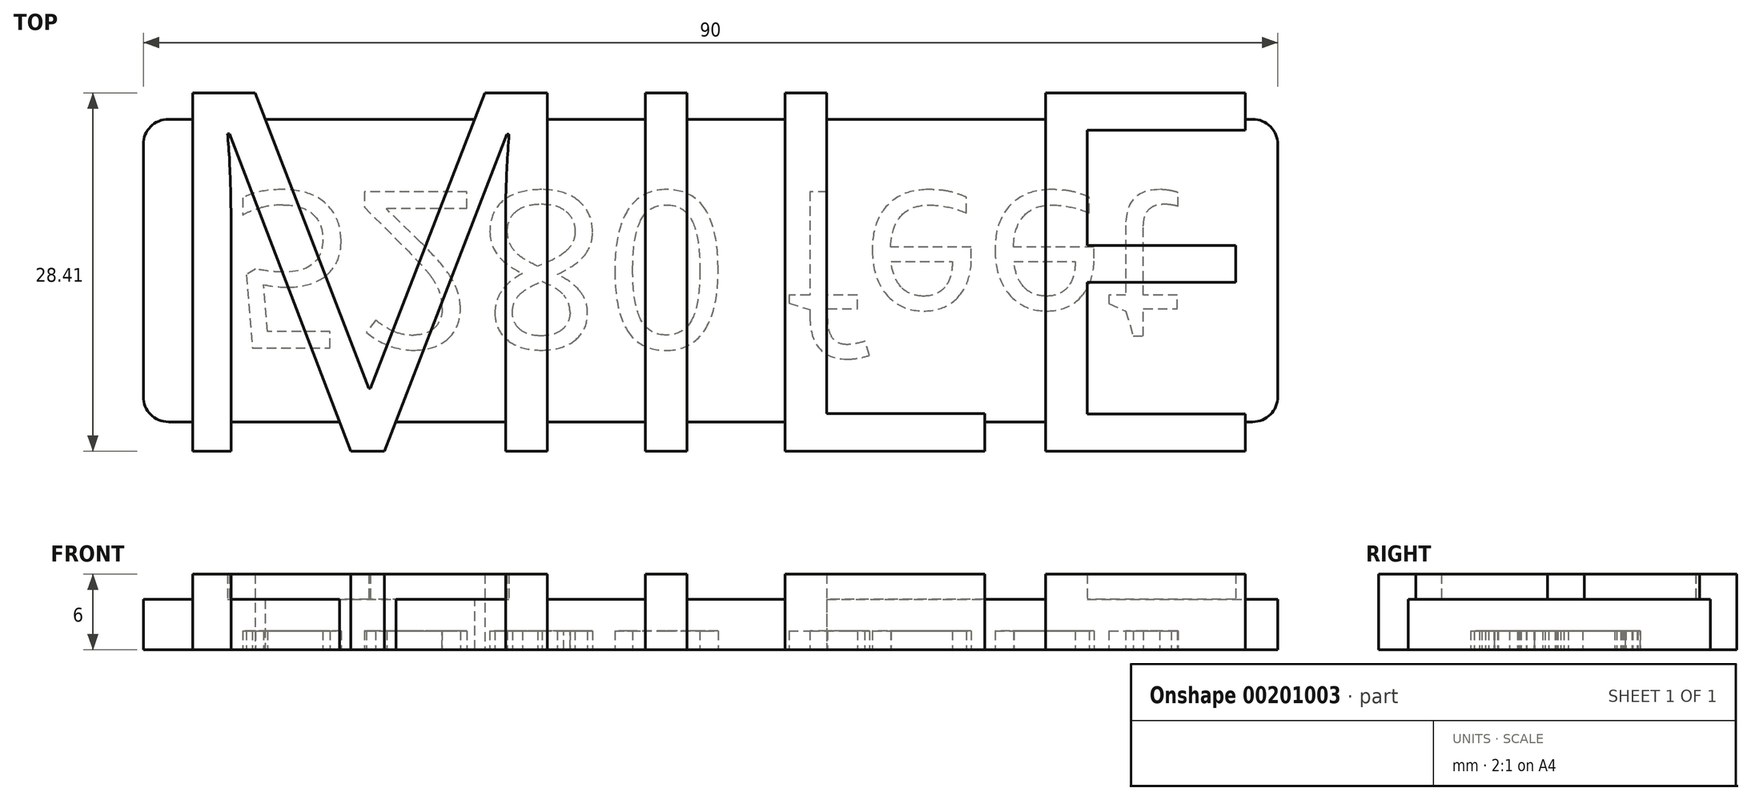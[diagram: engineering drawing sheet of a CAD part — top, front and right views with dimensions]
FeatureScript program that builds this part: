
annotation { "Feature Type Name" : "Feature", "Feature Type Description" : "" }
export const myFeature = defineFeature(function(context is Context, id is Id, definition is map)
    precondition{}
    {
        {
            var Q0;
            Q0=qCreatedBy(makeId("Top.planeOp"),FACE);
            var sketch = newSketch(context, id + "F0", { "sketchPlane" : qUnion([Q0])});
            skLineSegment(sketch, "E0.bottom", {"start": v(-45, 12) * mm, "end": v(45, 12) * mm});
            skLineSegment(sketch, "E0.top", {"start": v(-45, -12) * mm, "end": v(45, -12) * mm});
            skLineSegment(sketch, "E0.left", {"start": v(-45, 12) * mm, "end": v(-45, -12) * mm});
            skLineSegment(sketch, "E0.right", {"start": v(45, 12) * mm, "end": v(45, -12) * mm});
            skLineSegment(sketch, "E1", {"start": v(0, -12) * mm, "end": v(0, 12) * mm, "construction": true});
            skSolve(sketch);
        }
        {
            var Q0;
            Q0=makeQuery(id+"F0.imprint","IMPRINT",FACE,{"disambiguationData":[TD([[makeQuery(id+"F0.imprint","IMPRINT",EDGE,{"derivedFrom":sQuery(id+"F0.wireOp",EDGE,"E0.bottom")}),-1.0]])]});
            extrude(context, id + "F1", {"entities" : qUnion([Q0]), "depth" : 4 * mm});
        }
        {
            var Q0;
            Q0=makeQuery(id+"F1.opExtrude","SWEPT_EDGE",EDGE,{"disambiguationData":[OSD([sQuery(id+"F0.wireOp",EDGE,"E0.top"),sQuery(id+"F0.wireOp",EDGE,"E0.left")])]});
            var Q1;
            Q1=makeQuery(id+"F1.opExtrude","SWEPT_EDGE",EDGE,{"disambiguationData":[OSD([sQuery(id+"F0.wireOp",EDGE,"E0.bottom"),sQuery(id+"F0.wireOp",EDGE,"E0.right")])]});
            var Q2;
            Q2=makeQuery(id+"F1.opExtrude","SWEPT_EDGE",EDGE,{"disambiguationData":[OSD([sQuery(id+"F0.wireOp",EDGE,"E0.bottom"),sQuery(id+"F0.wireOp",EDGE,"E0.left")])]});
            var Q3;
            Q3=makeQuery(id+"F1.opExtrude","SWEPT_EDGE",EDGE,{"disambiguationData":[OSD([sQuery(id+"F0.wireOp",EDGE,"E0.top"),sQuery(id+"F0.wireOp",EDGE,"E0.right")])]});
            fillet(context, id + "F2", {"entities" : qUnion([Q0, Q1, Q2, Q3]), "radius" : 2 * mm, "tangentPropagation" : true, "allowEdgeOverflow" : false});
        }
        {
            var Q0;
            Q0=makeQuery(id+"F1.opExtrude","CAP_FACE",FACE,{"disambiguationData":[OSD([sQuery(id+"F0.wireOp",EDGE,"E0.bottom"),sQuery(id+"F0.wireOp",EDGE,"E0.top"),sQuery(id+"F0.wireOp",EDGE,"E0.left"),sQuery(id+"F0.wireOp",EDGE,"E0.right")])],"isStart":false});
            var sketch = newSketch(context, id + "F3", { "sketchPlane" : qUnion([Q0])});
            skText(sketch, "E2", { "text": "MILE", "fontName": "OpenSans-Regular.ttf"});
            const initialGuessF3  = {"E2": [-0.045, -0.01433, 1, 0, 0.02865]};
            skSetInitialGuess(sketch, initialGuessF3);
            skSolve(sketch);
        }
        {
            var Q0;
            {var subQ0=sQuery(id+"F3.wireOp",EDGE,"E2.sketch_text.stroke-4");Q0=makeQuery(id+"F3.imprint","IMPRINT",FACE,{"disambiguationData":[TD([[makeQuery(id+"F3.imprint","IMPRINT",EDGE,{"derivedFrom":subQ0}),-1.0]])]});}
            var Q1;
            {var subQ0=sQuery(id+"F3.wireOp",EDGE,"E2.sketch_text.stroke-3");var subQ1=sQuery(id+"F3.wireOp",EDGE,"E2.sketch_text.stroke-2");var subQ2=makeQuery(id+"F3.imprint","INTERSECT",VERTEX,{"derivedFrom":[subQ1,subQ0]});Q1=makeQuery(id+"F3.imprint","IMPRINT",FACE,{"disambiguationData":[TD([[makeQuery(id+"F3.imprint","IMPRINT",EDGE,{"disambiguationData":[TD([[subQ2,1.0]])],"derivedFrom":subQ1}),-1.0]])]});}
            var Q2;
            {var subQ1=sQuery(id+"F3.wireOp",EDGE,"E2.sketch_text.stroke-1");Q2=makeQuery(id+"F3.imprint","IMPRINT",FACE,{"disambiguationData":[TD([[makeQuery(id+"F3.imprint","IMPRINT",EDGE,{"derivedFrom":subQ1}),-1.0]])]});}
            var Q3;
            {var subQ0=sQuery(id+"F3.wireOp",EDGE,"E2.sketch_text.stroke-0");var subQ1=makeQuery(id+"F1.opExtrude","CAP_EDGE",EDGE,{"disambiguationData":[OSD([sQuery(id+"F0.wireOp",EDGE,"E0.top")])],"isStart":false});var subQ2=makeQuery(id+"F3.imprint","INTERSECT",VERTEX,{"derivedFrom":[subQ1,subQ0]});Q3=makeQuery(id+"F3.imprint","IMPRINT",FACE,{"disambiguationData":[TD([[makeQuery(id+"F3.imprint","IMPRINT",EDGE,{"disambiguationData":[TD([[subQ2,-1.0]])],"derivedFrom":subQ0}),-1.0]])]});}
            var Q4;
            {var subQ1=sQuery(id+"F3.wireOp",EDGE,"E2.sketch_text.stroke-8");Q4=makeQuery(id+"F3.imprint","IMPRINT",FACE,{"disambiguationData":[TD([[makeQuery(id+"F3.imprint","IMPRINT",EDGE,{"derivedFrom":subQ1}),-1.0]])]});}
            var Q5;
            {var subQ0=sQuery(id+"F3.wireOp",EDGE,"E2.sketch_text.stroke-9");var subQ1=makeQuery(id+"F1.opExtrude","CAP_EDGE",EDGE,{"disambiguationData":[OSD([sQuery(id+"F0.wireOp",EDGE,"E0.bottom")])],"isStart":false});var subQ2=makeQuery(id+"F3.imprint","INTERSECT",VERTEX,{"derivedFrom":[subQ1,subQ0]});Q5=makeQuery(id+"F3.imprint","IMPRINT",FACE,{"disambiguationData":[TD([[makeQuery(id+"F3.imprint","IMPRINT",EDGE,{"disambiguationData":[TD([[subQ2,1.0]])],"derivedFrom":subQ0}),-1.0]])]});}
            var Q6;
            {var subQ1=sQuery(id+"F3.wireOp",EDGE,"E2.sketch_text.stroke-10");Q6=makeQuery(id+"F3.imprint","IMPRINT",FACE,{"disambiguationData":[TD([[makeQuery(id+"F3.imprint","IMPRINT",EDGE,{"derivedFrom":subQ1}),-1.0]])]});}
            var Q7;
            {var subQ0=sQuery(id+"F3.wireOp",EDGE,"E2.sketch_text.stroke-11");var subQ1=makeQuery(id+"F1.opExtrude","CAP_EDGE",EDGE,{"disambiguationData":[OSD([sQuery(id+"F0.wireOp",EDGE,"E0.bottom")])],"isStart":false});var subQ2=makeQuery(id+"F3.imprint","INTERSECT",VERTEX,{"derivedFrom":[subQ1,subQ0]});Q7=makeQuery(id+"F3.imprint","IMPRINT",FACE,{"disambiguationData":[TD([[makeQuery(id+"F3.imprint","IMPRINT",EDGE,{"disambiguationData":[TD([[subQ2,-1.0]])],"derivedFrom":subQ0}),-1.0]])]});}
            var Q8;
            {var subQ0=sQuery(id+"F3.wireOp",EDGE,"E2.sketch_text.stroke-12");Q8=makeQuery(id+"F3.imprint","IMPRINT",FACE,{"disambiguationData":[TD([[makeQuery(id+"F3.imprint","IMPRINT",EDGE,{"derivedFrom":subQ0}),-1.0]])]});}
            var Q9;
            {var subQ0=sQuery(id+"F3.wireOp",EDGE,"E2.sketch_text.stroke-21");Q9=makeQuery(id+"F3.imprint","IMPRINT",FACE,{"disambiguationData":[TD([[makeQuery(id+"F3.imprint","IMPRINT",EDGE,{"derivedFrom":subQ0}),-1.0]])]});}
            var Q10;
            {var subQ0=sQuery(id+"F3.wireOp",EDGE,"E2.sketch_text.stroke-18");var subQ1=makeQuery(id+"F1.opExtrude","CAP_EDGE",EDGE,{"disambiguationData":[OSD([sQuery(id+"F0.wireOp",EDGE,"E0.top")])],"isStart":false});var subQ2=makeQuery(id+"F3.imprint","INTERSECT",VERTEX,{"derivedFrom":[subQ1,subQ0]});Q10=makeQuery(id+"F3.imprint","IMPRINT",FACE,{"disambiguationData":[TD([[makeQuery(id+"F3.imprint","IMPRINT",EDGE,{"disambiguationData":[TD([[subQ2,-1.0]])],"derivedFrom":subQ0}),-1.0]])]});}
            var Q11;
            {var subQ0=sQuery(id+"F3.wireOp",EDGE,"E2.sketch_text.stroke-19");Q11=makeQuery(id+"F3.imprint","IMPRINT",FACE,{"disambiguationData":[TD([[makeQuery(id+"F3.imprint","IMPRINT",EDGE,{"derivedFrom":subQ0}),-1.0]])]});}
            var Q12;
            {var subQ0=sQuery(id+"F3.wireOp",EDGE,"E2.sketch_text.stroke-25");Q12=makeQuery(id+"F3.imprint","IMPRINT",FACE,{"disambiguationData":[TD([[makeQuery(id+"F3.imprint","IMPRINT",EDGE,{"derivedFrom":subQ0}),-1.0]])]});}
            var Q13;
            {var subQ0=sQuery(id+"F3.wireOp",EDGE,"E2.sketch_text.stroke-22");var subQ1=makeQuery(id+"F1.opExtrude","CAP_EDGE",EDGE,{"disambiguationData":[OSD([sQuery(id+"F0.wireOp",EDGE,"E0.top")])],"isStart":false});var subQ2=makeQuery(id+"F3.imprint","INTERSECT",VERTEX,{"derivedFrom":[subQ1,subQ0]});Q13=makeQuery(id+"F3.imprint","IMPRINT",FACE,{"disambiguationData":[TD([[makeQuery(id+"F3.imprint","IMPRINT",EDGE,{"disambiguationData":[TD([[subQ2,-1.0]])],"derivedFrom":subQ0}),-1.0]])]});}
            var Q14;
            {var subQ0=sQuery(id+"F3.wireOp",EDGE,"E2.sketch_text.stroke-23");Q14=makeQuery(id+"F3.imprint","IMPRINT",FACE,{"disambiguationData":[TD([[makeQuery(id+"F3.imprint","IMPRINT",EDGE,{"derivedFrom":subQ0}),-1.0]])]});}
            var Q15;
            {var subQ5=sQuery(id+"F3.wireOp",EDGE,"E2.sketch_text.stroke-28");Q15=makeQuery(id+"F3.imprint","IMPRINT",FACE,{"disambiguationData":[TD([[makeQuery(id+"F3.imprint","IMPRINT",EDGE,{"derivedFrom":subQ5}),-1.0]])]});}
            var Q16;
            {var subQ0=sQuery(id+"F3.wireOp",EDGE,"E2.sketch_text.stroke-34");Q16=makeQuery(id+"F3.imprint","IMPRINT",FACE,{"disambiguationData":[TD([[makeQuery(id+"F3.imprint","IMPRINT",EDGE,{"derivedFrom":subQ0}),-1.0]])]});}
            var Q17;
            {var subQ0=sQuery(id+"F3.wireOp",EDGE,"E2.sketch_text.stroke-30");Q17=makeQuery(id+"F3.imprint","IMPRINT",FACE,{"disambiguationData":[TD([[makeQuery(id+"F3.imprint","IMPRINT",EDGE,{"derivedFrom":subQ0}),-1.0]])]});}
            var Q18;
            {var subQ0=sQuery(id+"F3.wireOp",EDGE,"E2.sketch_text.stroke-6");Q18=makeQuery(id+"F3.imprint","IMPRINT",FACE,{"disambiguationData":[TD([[makeQuery(id+"F3.imprint","IMPRINT",EDGE,{"derivedFrom":subQ0}),-1.0]])]});}
            var Q19;
            {var subQ0=sQuery(id+"F3.wireOp",EDGE,"E2.sketch_text.stroke-17");Q19=makeQuery(id+"F3.imprint","IMPRINT",FACE,{"disambiguationData":[TD([[makeQuery(id+"F3.imprint","IMPRINT",EDGE,{"derivedFrom":subQ0}),-1.0]])]});}
            var Q20;
            {var subQ0=sQuery(id+"F3.wireOp",EDGE,"E2.sketch_text.stroke-27");Q20=makeQuery(id+"F3.imprint","IMPRINT",FACE,{"disambiguationData":[TD([[makeQuery(id+"F3.imprint","IMPRINT",EDGE,{"derivedFrom":subQ0}),-1.0]])]});}
            extrude(context, id + "F4", {"entities" : qUnion([Q0, Q1, Q2, Q3, Q4, Q5, Q6, Q7, Q8, Q9, Q10, Q11, Q12, Q13, Q14, Q15, Q16, Q17, Q18, Q19, Q20]), "operationType" : NewBodyOperationType.ADD, "depth" : 2 * mm, "hasSecondDirection" : true, "secondDirectionOppositeDirection" : true, "secondDirectionDepth" : 4 * mm});
        }
        {
            var Q0;
            Q0=makeQuery(id+"F1.opExtrude","CAP_FACE",FACE,{"disambiguationData":[OSD([sQuery(id+"F0.wireOp",EDGE,"E0.bottom"),sQuery(id+"F0.wireOp",EDGE,"E0.top"),sQuery(id+"F0.wireOp",EDGE,"E0.left"),sQuery(id+"F0.wireOp",EDGE,"E0.right")])],"isStart":true});
            var sketch = newSketch(context, id + "F5", { "sketchPlane" : qUnion([Q0])});
            skText(sketch, "E3", { "text": "5280 feet", "fontName": "OpenSans-Regular.ttf"});
            const initialGuessF5  = {"E3": [-0.03824, -0.00625, 1, 0, 0.0125]};
            skSetInitialGuess(sketch, initialGuessF5);
            skSolve(sketch);
        }
        {
            var Q0;
            Q0=makeQuery(id+"F5.imprint","IMPRINT",FACE,{"disambiguationData":[TD([[makeQuery(id+"F5.imprint","IMPRINT",EDGE,{"derivedFrom":sQuery(id+"F5.wireOp",EDGE,"E3.sketch_text.stroke-141")}),-1.0]])]});
            var Q1;
            Q1=makeQuery(id+"F5.imprint","IMPRINT",FACE,{"disambiguationData":[TD([[makeQuery(id+"F5.imprint","IMPRINT",EDGE,{"derivedFrom":sQuery(id+"F5.wireOp",EDGE,"E3.sketch_text.stroke-122")}),-1.0]])]});
            var Q2;
            Q2=makeQuery(id+"F5.imprint","IMPRINT",FACE,{"disambiguationData":[TD([[makeQuery(id+"F5.imprint","IMPRINT",EDGE,{"derivedFrom":sQuery(id+"F5.wireOp",EDGE,"E3.sketch_text.stroke-103")}),-1.0]])]});
            var Q3;
            Q3=makeQuery(id+"F5.imprint","IMPRINT",FACE,{"disambiguationData":[TD([[makeQuery(id+"F5.imprint","IMPRINT",EDGE,{"derivedFrom":sQuery(id+"F5.wireOp",EDGE,"E3.sketch_text.stroke-86")}),-1.0]])]});
            var Q4;
            Q4=makeQuery(id+"F5.imprint","IMPRINT",FACE,{"disambiguationData":[TD([[makeQuery(id+"F5.imprint","IMPRINT",EDGE,{"derivedFrom":sQuery(id+"F5.wireOp",EDGE,"E3.sketch_text.stroke-70")}),-1.0]])]});
            var Q5;
            Q5=makeQuery(id+"F5.imprint","IMPRINT",FACE,{"disambiguationData":[TD([[makeQuery(id+"F5.imprint","IMPRINT",EDGE,{"derivedFrom":sQuery(id+"F5.wireOp",EDGE,"E3.sketch_text.stroke-39")}),-1.0]])]});
            var Q6;
            Q6=makeQuery(id+"F5.imprint","IMPRINT",FACE,{"disambiguationData":[TD([[makeQuery(id+"F5.imprint","IMPRINT",EDGE,{"derivedFrom":sQuery(id+"F5.wireOp",EDGE,"E3.sketch_text.stroke-19")}),-1.0]])]});
            var Q7;
            Q7=makeQuery(id+"F5.imprint","IMPRINT",FACE,{"disambiguationData":[TD([[makeQuery(id+"F5.imprint","IMPRINT",EDGE,{"derivedFrom":sQuery(id+"F5.wireOp",EDGE,"E3.sketch_text.stroke-0")}),-1.0]])]});
            extrude(context, id + "F6", {"entities" : qUnion([Q0, Q1, Q2, Q3, Q4, Q5, Q6, Q7]), "operationType" : NewBodyOperationType.REMOVE, "oppositeDirection" : true, "depth" : 1.5 * mm});
        }
    });
